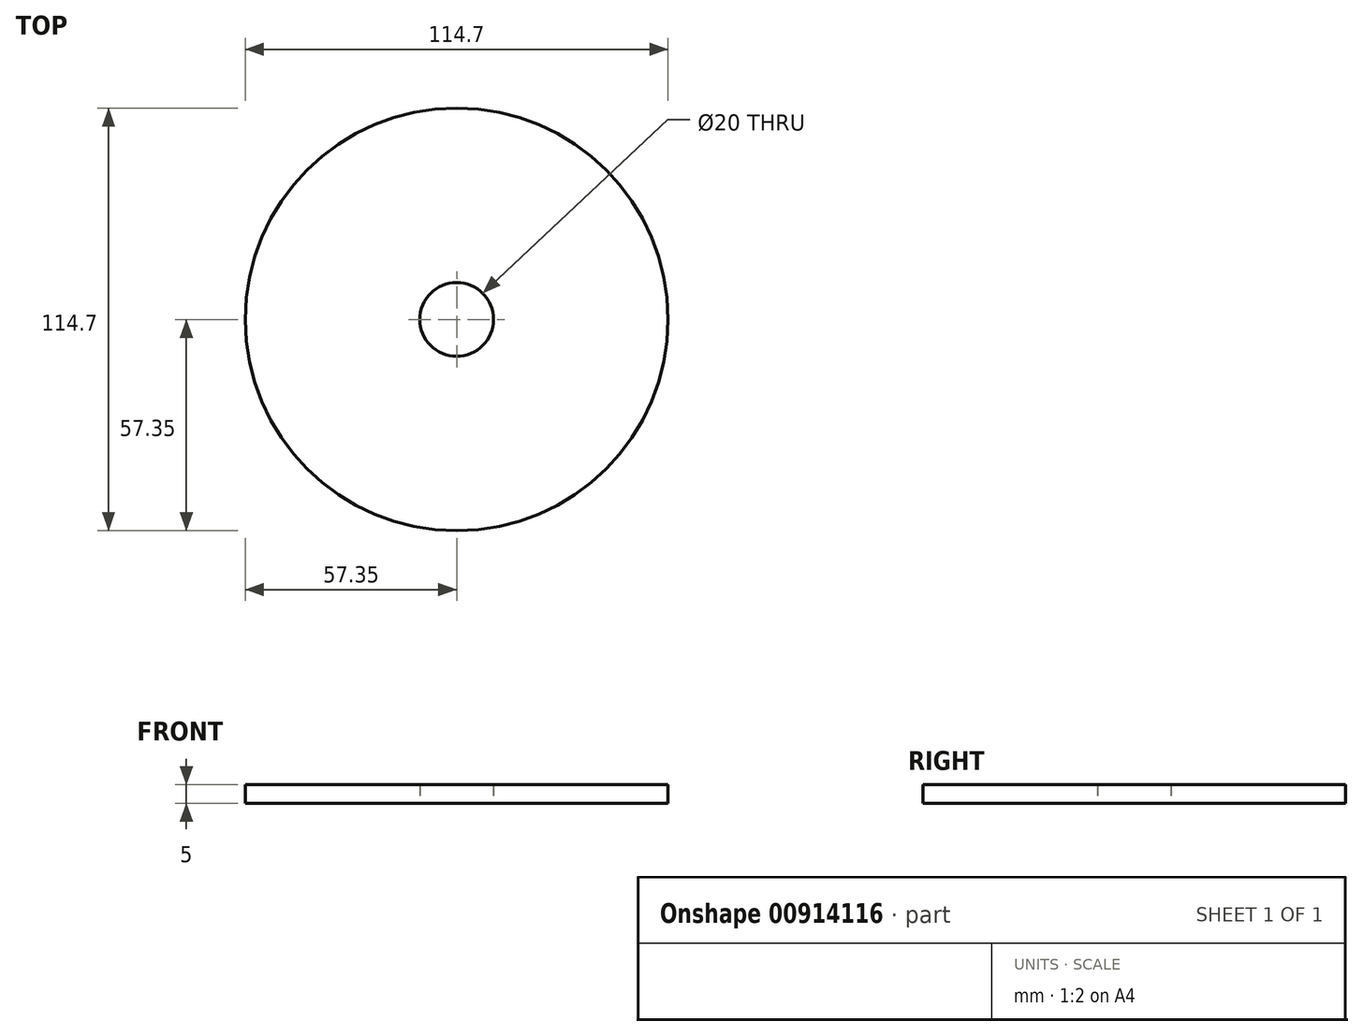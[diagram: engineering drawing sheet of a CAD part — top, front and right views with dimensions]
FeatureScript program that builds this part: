
annotation { "Feature Type Name" : "Feature", "Feature Type Description" : "" }
export const myFeature = defineFeature(function(context is Context, id is Id, definition is map)
    precondition{}
    {
        {
            var Q0;
            Q0=qCreatedBy(makeId("Top.planeOp"),FACE);
            var sketch = newSketch(context, id + "F0", { "sketchPlane" : qUnion([Q0])});
            skCircle(sketch, "E0", {"center": v(0, 0) * mm, "radius": 57.35 * mm});
            skCircle(sketch, "E1", {"center": v(0, 0) * mm, "radius": 10 * mm});
            skSolve(sketch);
        }
        {
            var Q0;
            Q0=makeQuery(id+"F0.imprint","IMPRINT",FACE,{"disambiguationData":[TD([[makeQuery(id+"F0.imprint","IMPRINT",EDGE,{"derivedFrom":sQuery(id+"F0.wireOp",EDGE,"E0")}),1.0]])]});
            extrude(context, id + "F1", {"entities" : qUnion([Q0]), "depth" : 5 * mm, "offsetDistance" : 25 * mm});
        }
    });
